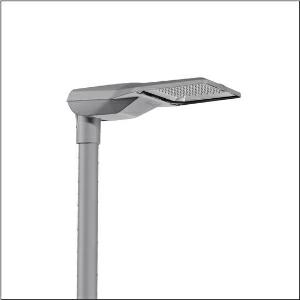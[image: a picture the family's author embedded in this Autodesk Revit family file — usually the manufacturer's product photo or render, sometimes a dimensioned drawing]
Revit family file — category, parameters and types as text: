
# Revit family: streetlight_sl_21_iq_midi___stw1_0a_5xe3e21d08nb_941d
name_source: partatom
category: Lighting Fixtures
units: mm (PartAtom-declared; Revit-internal decimal feet)

## family parameters
Cut with Voids When Loaded = No
Host = Face
Light Source = No
Part Type = Normal
Room Calculation Point = No
Round Connector Dimension = Use Diameter
Shared = No

## types (1)
- --- (1 x LED, 19210 lm, 155.5 W, 2200K)
    Apparent Load = 155 VA
    CIE Flux Codes = 39 75 98 100 100
    Color Rendering = 70
    Color Temperature = 2200K
    Default Elevation = 1800 mm
    Description = Streetlight SL 21 iQ midi, mast luminaire, primary light control with lens, of PMMA, primary optical cover: cover, of toughened safety glass, transparent, light distribution: STW1.0a, light emission: direct distribution, primary light characteristic: asymmetric, installation type: post-top, side-entry, LED, High Power LED, rated luminous flux: 19.210lm, luminous efficacy: 124lm/W, light colour: 722, colour temperature: 2200K, control: Auto-Match, Temp-Guard, Lumen-Switch, Night-Set, Smart-Wire, Light-Fading, Desk-Remote (wireless, voltage-free reading and setting of iQ features in the workshop via application-optimized NFC function/RFID function), optimised constant luminous flux control (CLO 2.0), presetting dimming linear, mains connection: 230..240V, AC, 50/60Hz, start of lifetime: 156W, end of service life: 162W, reduction: 69W, luminaire housing, of diecast aluminium, powder-coated, Siteco® metallic grey (DB 702S), corrosivity category C5 mid according to DIN EN ISO 12944, please order mast flange separately, inclination adjustable: 0°, 5°, 10°, 15°, sealing non-destructively replaceable, multi-level sealing system, length: 644mm, width: 335mm, height: 110mm, mast flange for spigot size: 42mm (side-entry): 5XC10008XM4, 60/48mm (side-entry/post-top): 5XC10108XM2, 76/60mm (side-entry/post-top): 5XC10108XM1, protection rating (complete): IP66, insulation class (complete): insulation class II (safety insulation), certification: CE, ENEC, ENEC+, VDE, impact resistance: IK09, permissible operating ambient temperature for outdoor applications: -40..+50°C, standard-compliant lighting for roads and squares, packaging unit: 1 piece

Light Distribution: STW1.0a
    Height = 111 mm
    Lamp = 1 x LED
    Lamp Light Flux = 19210 lm
    Lamp Power = 155.5 W
    Lamp count = 1
    Length = 644 mm
    Luminous efficacy = 124 lm/W
    Manufacturer = Siteco
    ModVariant = No
    Model = 5XE3E21D08NB
    Number of Poles = 1
    OnlyDefault = Yes
    Power Factor = 1
    Product Name = Streetlight SL 21 iQ midi | STW1.0a
    Product group = mast luminaire | pylon top
    ProductGroupID = 6100
    Protection Class = Protection class II
    Protection Degree = IP 66
    RLX_Detail_Level = 1
    RLX_Emergency_Light_Flux = 0 lm
    RLX_Emergency_Type = 0
    RLX_Emergency_Type_DB = No
    RlxData = <blob elided: 91165 chars, md5=e0fdd20a>
    Socket = socket
    Standby Power = 0 W
    System Light Flux = 19210 lm
    System Power = 155 W
    Type Comments = factory setting: luminous flux: 100 % | dim-lin: 254 | 823 mA
    Type Image = l_1004298.jpg
    URL = http://relux.com
    VarID = @adj_102585
    Voltage = 0 V
    Weight = 0.00 kg
    Width = 336 mm

## geometry (parser evidence)
native form markers: Blend x4, Sweep x12
no freeform markers — native parametric forms only
